# Revit family: Термостатическая головка HERZ, с присоединительной резьбой М 28х1.5, 7230
name_source: partatom
category: Rohrzubehör
units: mm (PartAtom-declared; Revit-internal decimal feet)

## family parameters
Arbeitsebenenbasiert = Nein
Beim Laden mit Abzugskörper schneiden = Nein
Bemaßung runder Anschluss = Durchmesser verwenden
Gemeinsam genutzt = Nein
Immer vertikal = Nein
OmniClass-Nummer = 23.65.55.14
OmniClass-Titel = Valves for Liquid Services
Teiletyp = Normal

## types (1)
- Термостатическая головка HERZ, с присоединительной резьбой М 28х1.5, 7230
    H01 = 34 mm
    H02 = 17 mm
    H03 = 5.5 mm  [stored 0.0180446 ft]
    H05 = 10.5 mm  [stored 0.0344488 ft]
    H06 = 3 mm  [stored 0.00984252 ft]
    H07 = 59 mm  [stored 0.19357 ft]
    H08 = 10 mm  [stored 0.0328084 ft]
    H09 = 3.5 mm  [stored 0.0114829 ft]
    Hersteller = HERZ Armaturen Ges.m.b.H.
    R01 = 22.4 mm  [stored 0.0734908 ft]
    R02 = 12.2 mm
    R03 = 13.2 mm  [stored 0.0433071 ft]
    R04 = 14.75 mm
    R05 = 16.35 mm  [stored 0.0536417 ft]
    R06 = 24 mm  [stored 0.0787402 ft]
    R07 = 6 mm  [stored 0.019685 ft]
    S01 = 76 mm  [stored 0.249344 ft]
    S02 = 60 mm
    URL = www.herz-armaturen.ru
    Vorgabe-Ansicht = 0 mm  [stored 0 ft]
    W01 = 135.00°
    W02 = 120.00°
    Автоматическая защита от замерзания = при прибл. 6 °C
    Диапазон регулирования = 0 - 28°C
    Исполнение = Термостатическая головка с жидкостным датчиком (гидросенсором) с позициями теплового запираниия "0" и морозозащиты, с ограничением и блокировкой диапазона регулирования. Цвет маховика - белый.
    Маховик = Пластик, белый
    Номер заказа = 1723006
    Область применения = Для монтажа на всех HERZ-клапанах, предназначенных для термостатической работы.
    Принцип действия = HERZ-термостатическая головка является датчиком прямого регулирования.
Изменение объема жидкости в HERZ-гидросенсоре приводит в движение шток клапана.

note: [stored X ft] marks values corroborated as IEEE doubles in the binary element streams (Revit-internal decimal feet)
